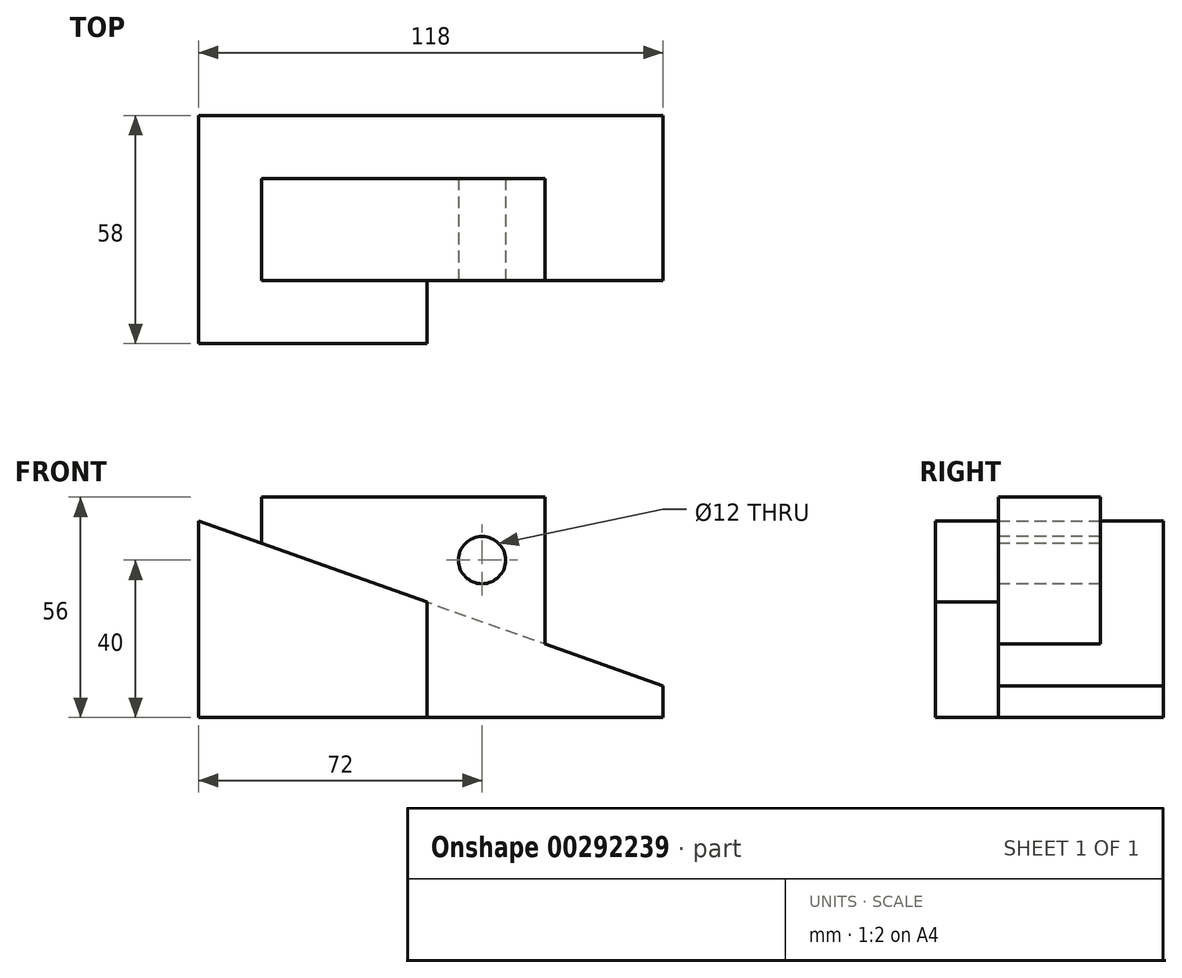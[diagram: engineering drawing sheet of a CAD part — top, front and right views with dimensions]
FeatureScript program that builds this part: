
annotation { "Feature Type Name" : "Feature", "Feature Type Description" : "" }
export const myFeature = defineFeature(function(context is Context, id is Id, definition is map)
    precondition{}
    {
        {
            var Q0;
            Q0=qCreatedBy(makeId("Front.planeOp"),FACE);
            var sketch = newSketch(context, id + "F0", { "sketchPlane" : qUnion([Q0])});
            skLineSegment(sketch, "E0", {"start": v(0, 0) * mm, "end": v(118, 0) * mm});
            skLineSegment(sketch, "E1", {"start": v(118, 0) * mm, "end": v(118, 8) * mm});
            skLineSegment(sketch, "E2", {"start": v(0, 0) * mm, "end": v(0, 50) * mm});
            skLineSegment(sketch, "E3", {"start": v(0, 50) * mm, "end": v(118, 8) * mm});
            skSolve(sketch);
        }
        {
            var Q0;
            Q0=makeQuery(id+"F0.imprint","IMPRINT",FACE,{"disambiguationData":[TD([[makeQuery(id+"F0.imprint","IMPRINT",EDGE,{"derivedFrom":sQuery(id+"F0.wireOp",EDGE,"E0")}),1.0]])]});
            extrude(context, id + "F1", {"entities" : qUnion([Q0]), "depth" : 58 * mm});
        }
        {
            var Q0;
            Q0=qCreatedBy(makeId("Top.planeOp"),FACE);
            cPlane(context, id + "F2", {"entities" : qUnion([Q0]), "cplaneType" : CPlaneType.OFFSET, "offset" : 56 * mm, "width" : 150 * mm, "height" : 150 * mm});
        }
        {
            var Q0;
            Q0=qCreatedBy(id+"F2.planeOp",FACE);
            var sketch = newSketch(context, id + "F3", { "sketchPlane" : qUnion([Q0])});
            skLineSegment(sketch, "E4.bottom", {"start": v(16, -16) * mm, "end": v(88, -16) * mm});
            skLineSegment(sketch, "E4.top", {"start": v(16, -42) * mm, "end": v(88, -42) * mm});
            skLineSegment(sketch, "E4.left", {"start": v(16, -16) * mm, "end": v(16, -42) * mm});
            skLineSegment(sketch, "E4.right", {"start": v(88, -16) * mm, "end": v(88, -42) * mm});
            skSolve(sketch);
        }
        {
            var Q0;
            Q0=makeQuery(id+"F3.imprint","IMPRINT",FACE,{"disambiguationData":[TD([[makeQuery(id+"F3.imprint","IMPRINT",EDGE,{"derivedFrom":sQuery(id+"F3.wireOp",EDGE,"E4.bottom")}),-1.0]])]});
            var Q1;
            Q1=makeQuery(id+"F1.opExtrude","SWEPT_FACE",FACE,{"disambiguationData":[OSD([sQuery(id+"F0.wireOp",EDGE,"E3")])]});
            extrude(context, id + "F4", {"entities" : qUnion([Q0]), "operationType" : NewBodyOperationType.ADD, "endBound" : BoundingType.UP_TO_SURFACE, "oppositeDirection" : true, "endBoundEntityFace" : qUnion([Q1]), "depth" : 25 * mm});
        }
        {
            var Q0;
            Q0=qCreatedBy(id+"F2.planeOp",FACE);
            var sketch = newSketch(context, id + "F5", { "sketchPlane" : qUnion([Q0])});
            skLineSegment(sketch, "E5.bottom", {"start": v(58, -42) * mm, "end": v(118, -42) * mm});
            skLineSegment(sketch, "E5.top", {"start": v(58, -58) * mm, "end": v(118, -58) * mm});
            skLineSegment(sketch, "E5.left", {"start": v(58, -42) * mm, "end": v(58, -58) * mm});
            skLineSegment(sketch, "E5.right", {"start": v(118, -42) * mm, "end": v(118, -58) * mm});
            skSolve(sketch);
        }
        {
            var Q0;
            Q0=makeQuery(id+"F5.imprint","IMPRINT",FACE,{"disambiguationData":[TD([[makeQuery(id+"F5.imprint","IMPRINT",EDGE,{"derivedFrom":sQuery(id+"F5.wireOp",EDGE,"E5.bottom")}),-1.0]])]});
            extrude(context, id + "F6", {"entities" : qUnion([Q0]), "operationType" : NewBodyOperationType.REMOVE, "endBound" : BoundingType.THROUGH_ALL, "oppositeDirection" : true, "depth" : 25 * mm});
        }
        {
            var Q0;
            Q0=makeQuery(id+"F6.boolean.opBoolean","MERGE",FACE,{"derivedFrom":[makeQuery(id+"F4.opExtrude","SWEPT_FACE",FACE,{"disambiguationData":[OSD([sQuery(id+"F3.wireOp",EDGE,"E4.top")])]}),makeQuery(id+"F6.opExtrude","SWEPT_FACE",FACE,{"disambiguationData":[OSD([sQuery(id+"F5.wireOp",EDGE,"E5.bottom")])]})]});
            var sketch = newSketch(context, id + "F7", { "sketchPlane" : qUnion([Q0])});
            skCircle(sketch, "E6", {"center": v(72, 40) * mm, "radius": 6 * mm});
            skSolve(sketch);
        }
        {
            var Q0;
            Q0=makeQuery(id+"F7.imprint","IMPRINT",FACE,{"disambiguationData":[TD([[makeQuery(id+"F7.imprint","IMPRINT",EDGE,{"derivedFrom":sQuery(id+"F7.wireOp",EDGE,"E6")}),1.0]])]});
            extrude(context, id + "F8", {"entities" : qUnion([Q0]), "operationType" : NewBodyOperationType.REMOVE, "endBound" : BoundingType.THROUGH_ALL, "oppositeDirection" : true, "depth" : 25 * mm});
        }
    });
